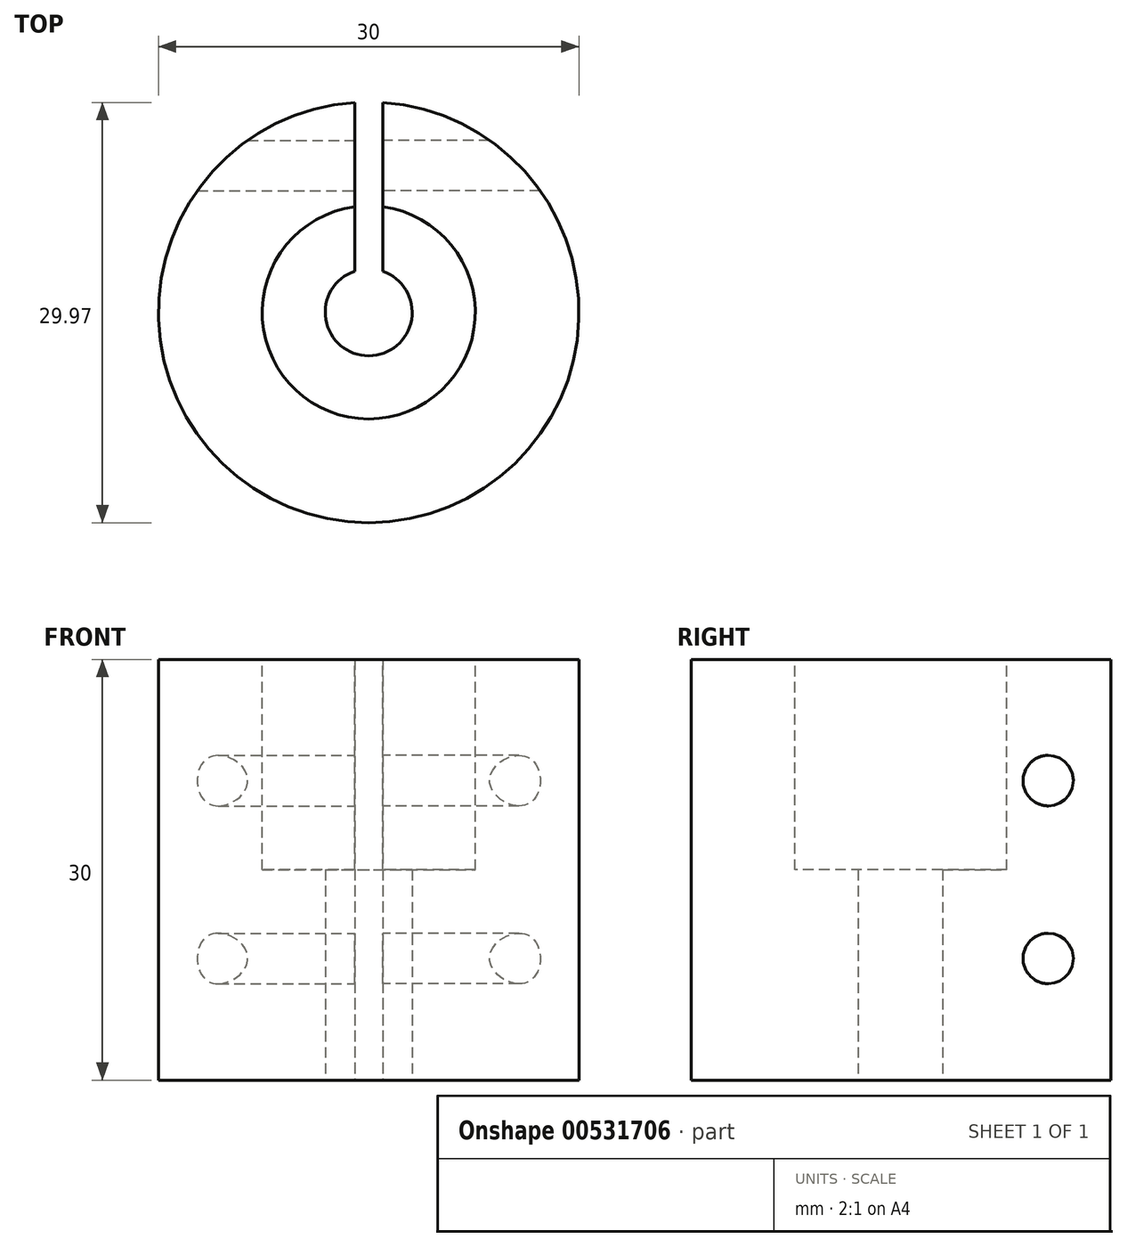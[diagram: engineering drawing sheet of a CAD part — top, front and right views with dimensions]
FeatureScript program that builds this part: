
annotation { "Feature Type Name" : "Feature", "Feature Type Description" : "" }
export const myFeature = defineFeature(function(context is Context, id is Id, definition is map)
    precondition{}
    {
        {
            var Q0;
            Q0=qCreatedBy(makeId("Top.planeOp"),FACE);
            var sketch = newSketch(context, id + "F0", { "sketchPlane" : qUnion([Q0])});
            skCircle(sketch, "E0", {"center": v(0, 0) * mm, "radius": 15 * mm});
            skSolve(sketch);
        }
        {
            var Q0;
            Q0 = qSketchRegion(id + "F0", true);
            extrude(context, id + "F1", {"entities" : qUnion([Q0]), "depth" : 30 * mm, "offsetDistance" : 25.4 * mm});
        }
        {
            var Q0;
            Q0=makeQuery(id+"F1.opExtrude","CAP_FACE",FACE,{"disambiguationData":[OSD([sQuery(id+"F0.wireOp",EDGE,"E0")])],"isStart":false});
            var sketch = newSketch(context, id + "F2", { "sketchPlane" : qUnion([Q0])});
            skCircle(sketch, "E1", {"center": v(0, 0) * mm, "radius": 7.6 * mm});
            skSolve(sketch);
        }
        {
            var Q0;
            Q0 = qSketchRegion(id + "F2", true);
            extrude(context, id + "F3", {"entities" : qUnion([Q0]), "operationType" : NewBodyOperationType.REMOVE, "oppositeDirection" : true, "depth" : 15 * mm, "offsetDistance" : 25.4 * mm});
        }
        {
            var Q0;
            Q0=makeQuery(id+"F1.opExtrude","CAP_FACE",FACE,{"disambiguationData":[OSD([sQuery(id+"F0.wireOp",EDGE,"E0")])],"isStart":true});
            var sketch = newSketch(context, id + "F4", { "sketchPlane" : qUnion([Q0])});
            skCircle(sketch, "E2", {"center": v(0, 0) * mm, "radius": 3.1 * mm});
            skSolve(sketch);
        }
        {
            var Q0;
            Q0 = qSketchRegion(id + "F4", true);
            extrude(context, id + "F5", {"entities" : qUnion([Q0]), "operationType" : NewBodyOperationType.REMOVE, "oppositeDirection" : true, "depth" : 25.4 * mm, "offsetDistance" : 25.4 * mm});
        }
        {
            var Q0;
            Q0=makeQuery(id+"F1.opExtrude","CAP_FACE",FACE,{"disambiguationData":[OSD([sQuery(id+"F0.wireOp",EDGE,"E0")])],"isStart":true});
            var sketch = newSketch(context, id + "F6", { "sketchPlane" : qUnion([Q0])});
            skLineSegment(sketch, "E3.bottom", {"start": v(-1, -19.53) * mm, "end": v(1, -19.53) * mm});
            skLineSegment(sketch, "E3.top", {"start": v(-1, 19.53) * mm, "end": v(1, 19.53) * mm});
            skLineSegment(sketch, "E3.left", {"start": v(-1, -19.53) * mm, "end": v(-1, 19.53) * mm});
            skLineSegment(sketch, "E3.right", {"start": v(1, -19.53) * mm, "end": v(1, 19.53) * mm});
            skPoint(sketch, "E3.middle", {"position": v(0, 0) * mm});
            skLineSegment(sketch, "E4", {"start": v(1, 0) * mm, "end": v(-1, 0) * mm});
            skSolve(sketch);
        }
        {
            var Q0;
            {var subQ0=sQuery(id+"F6.wireOp",EDGE,"E3.bottom");Q0=makeQuery(id+"F6.imprint","IMPRINT",FACE,{"disambiguationData":[TD([[makeQuery(id+"F6.imprint","IMPRINT",EDGE,{"derivedFrom":subQ0}),1.0]])]});}
            var Q1;
            {var subQ0=sQuery(id+"F6.wireOp",EDGE,"E4");Q1=makeQuery(id+"F6.imprint","IMPRINT",FACE,{"disambiguationData":[TD([[makeQuery(id+"F6.imprint","IMPRINT",EDGE,{"derivedFrom":subQ0}),1.0]])]});}
            var Q2;
            {var subQ0=sQuery(id+"F6.wireOp",EDGE,"E3.left");var subQ1=makeQuery(id+"F1.opExtrude","CAP_EDGE",EDGE,{"disambiguationData":[OSD([sQuery(id+"F0.wireOp",EDGE,"E0")])],"isStart":true});var subQ2=makeQuery(id+"F6.imprint","INTERSECT",VERTEX,{"disambiguationData":[OD(0.0)],"derivedFrom":[subQ1,subQ0]});Q2=makeQuery(id+"F6.imprint","IMPRINT",FACE,{"disambiguationData":[TD([[makeQuery(id+"F6.imprint","IMPRINT",EDGE,{"disambiguationData":[TD([[subQ2,-1.0]])],"derivedFrom":subQ0}),-1.0]])]});}
            extrude(context, id + "F7", {"entities" : qUnion([Q0, Q1, Q2]), "operationType" : NewBodyOperationType.REMOVE, "oppositeDirection" : true, "depth" : 50.8 * mm, "offsetDistance" : 25.4 * mm});
        }
        {
            var Q0;
            Q0=qCreatedBy(makeId("Right.planeOp"),FACE);
            var sketch = newSketch(context, id + "F8", { "sketchPlane" : qUnion([Q0])});
            skLineSegment(sketch, "E5.bottom", {"start": v(0, 0) * mm, "end": v(10.48, 0) * mm});
            skLineSegment(sketch, "E5.top", {"start": v(0, 8.68) * mm, "end": v(10.48, 8.68) * mm});
            skLineSegment(sketch, "E5.left", {"start": v(0, 0) * mm, "end": v(0, 8.68) * mm});
            skLineSegment(sketch, "E5.right", {"start": v(10.48, 0) * mm, "end": v(10.48, 8.68) * mm});
            skLineSegment(sketch, "E6", {"start": v(10.48, 8.68) * mm, "end": v(10.48, 21.36) * mm});
            skCircle(sketch, "E7", {"center": v(10.48, 8.68) * mm, "radius": 1.8 * mm});
            skCircle(sketch, "E8", {"center": v(10.48, 21.36) * mm, "radius": 1.8 * mm});
            skSolve(sketch);
        }
        {
            var Q0;
            {var subQ0=sQuery(id+"F8.wireOp",EDGE,"E6");var subQ3=sQuery(id+"F8.wireOp",EDGE,"E7");var subQ5=makeQuery(id+"F8.imprint","INTERSECT",VERTEX,{"derivedFrom":[subQ0,subQ3]});Q0=makeQuery(id+"F8.imprint","IMPRINT",FACE,{"disambiguationData":[TD([[makeQuery(id+"F8.imprint","IMPRINT",EDGE,{"disambiguationData":[TD([[subQ5,1.0]])],"derivedFrom":subQ3}),1.0]])]});}
            var Q1;
            {var subQ0=sQuery(id+"F8.wireOp",EDGE,"E6");var subQ3=sQuery(id+"F8.wireOp",EDGE,"E7");var subQ5=makeQuery(id+"F8.imprint","INTERSECT",VERTEX,{"derivedFrom":[subQ0,subQ3]});Q1=makeQuery(id+"F8.imprint","IMPRINT",FACE,{"disambiguationData":[TD([[makeQuery(id+"F8.imprint","IMPRINT",EDGE,{"disambiguationData":[TD([[subQ5,-1.0]])],"derivedFrom":subQ3}),1.0]])]});}
            var Q2;
            {var subQ1=sQuery(id+"F8.wireOp",EDGE,"E5.top");var subQ3=sQuery(id+"F8.wireOp",EDGE,"E7");var subQ4=makeQuery(id+"F8.imprint","INTERSECT",VERTEX,{"derivedFrom":[subQ1,subQ3]});Q2=makeQuery(id+"F8.imprint","IMPRINT",FACE,{"disambiguationData":[TD([[makeQuery(id+"F8.imprint","IMPRINT",EDGE,{"disambiguationData":[TD([[subQ4,-1.0]])],"derivedFrom":subQ3}),1.0]])]});}
            var Q3;
            Q3=makeQuery(id+"F8.imprint","IMPRINT",FACE,{"disambiguationData":[TD([[makeQuery(id+"F8.imprint","IMPRINT",EDGE,{"derivedFrom":sQuery(id+"F8.wireOp",EDGE,"E8")}),1.0]])]});
            extrude(context, id + "F9", {"entities" : qUnion([Q0, Q1, Q2, Q3]), "operationType" : NewBodyOperationType.REMOVE, "endBound" : BoundingType.THROUGH_ALL, "oppositeDirection" : true, "depth" : 25.4 * mm, "offsetDistance" : 25.4 * mm});
        }
        {
            var Q0;
            Q0=makeQuery(id+"F7.boolean.opBoolean","COPY",FACE,{"derivedFrom":makeQuery(id+"F7.opExtrude","SWEPT_FACE",FACE,{"disambiguationData":[OSD([sQuery(id+"F6.wireOp",EDGE,"E3.left")])]})});
            var sketch = newSketch(context, id + "F10", { "sketchPlane" : qUnion([Q0])});
            skSolve(sketch);
        }
        {
            var Q0;
            Q0 = qSketchRegion(id + "F10", true);
            var Q1;
            Q1=makeQuery(id+"F10.imprint","IMPRINT",FACE,{"disambiguationData":[TD([[makeQuery(id+"F10.imprint","IMPRINT",EDGE,{"derivedFrom":makeQuery(id+"F9.boolean.opBoolean","INTERSECT",EDGE,{"derivedFrom":[makeQuery(id+"F7.boolean.opBoolean","COPY",FACE,{"derivedFrom":makeQuery(id+"F7.opExtrude","SWEPT_FACE",FACE,{"disambiguationData":[OSD([sQuery(id+"F6.wireOp",EDGE,"E3.left")])]})}),makeQuery(id+"F9.opExtrude","SWEPT_FACE",FACE,{"disambiguationData":[OSD([sQuery(id+"F8.wireOp",EDGE,"E7")])]})]})}),1.0]])]});
            var Q2;
            Q2=makeQuery(id+"F10.imprint","IMPRINT",FACE,{"disambiguationData":[TD([[makeQuery(id+"F10.imprint","IMPRINT",EDGE,{"derivedFrom":makeQuery(id+"F9.boolean.opBoolean","INTERSECT",EDGE,{"derivedFrom":[makeQuery(id+"F7.boolean.opBoolean","COPY",FACE,{"derivedFrom":makeQuery(id+"F7.opExtrude","SWEPT_FACE",FACE,{"disambiguationData":[OSD([sQuery(id+"F6.wireOp",EDGE,"E3.left")])]})}),makeQuery(id+"F9.opExtrude","SWEPT_FACE",FACE,{"disambiguationData":[OSD([sQuery(id+"F8.wireOp",EDGE,"E8")])]})]})}),1.0]])]});
            extrude(context, id + "F11", {"entities" : qUnion([Q0, Q1, Q2]), "operationType" : NewBodyOperationType.REMOVE, "depth" : 25.4 * mm, "offsetDistance" : 25.4 * mm});
        }
    });
